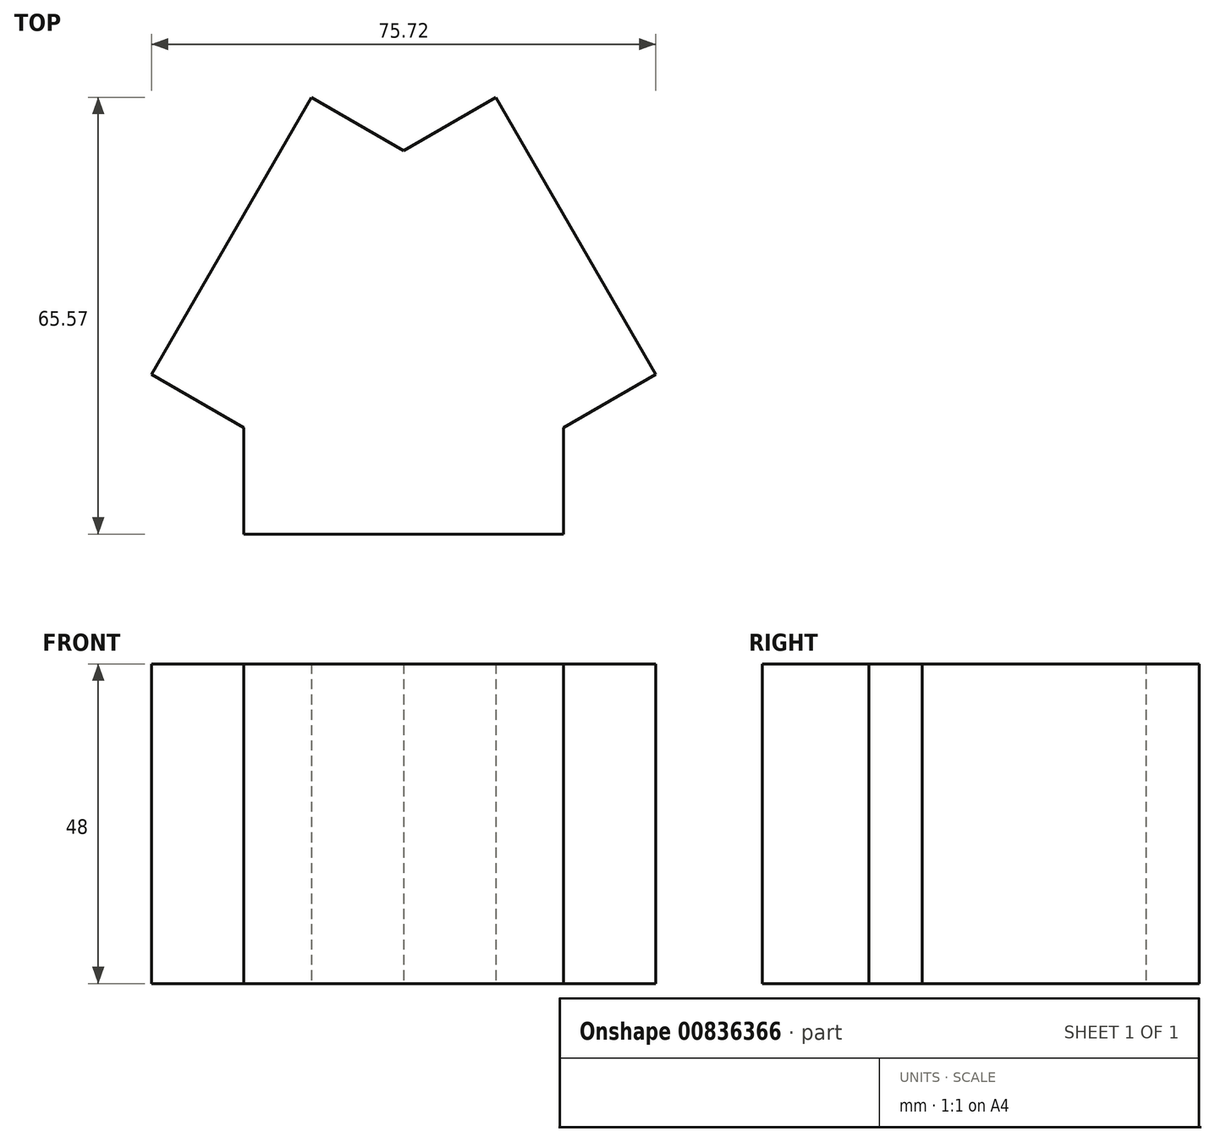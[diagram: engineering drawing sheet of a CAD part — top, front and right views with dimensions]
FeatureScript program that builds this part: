
annotation { "Feature Type Name" : "Feature", "Feature Type Description" : "" }
export const myFeature = defineFeature(function(context is Context, id is Id, definition is map)
    precondition{}
    {
        {
            var Q0;
            Q0=qCreatedBy(makeId("Top.planeOp"),FACE);
            var sketch = newSketch(context, id + "F0", { "sketchPlane" : qUnion([Q0])});
            skCircle(sketch, "E0.cCircle", {"center": v(0, 0) * mm, "radius": 13.86 * mm, "construction": true});
            skLineSegment(sketch, "E0.0", {"start": v(0, 27.71) * mm, "end": v(24, -13.86) * mm});
            skLineSegment(sketch, "E0.1", {"start": v(24, -13.86) * mm, "end": v(-24, -13.86) * mm});
            skLineSegment(sketch, "E0.2", {"start": v(-24, -13.86) * mm, "end": v(0, 27.71) * mm});
            skPoint(sketch, "E0.0.midPoint", {"position": v(12, 6.93) * mm});
            skSolve(sketch);
        }
        {
            var Q0;
            Q0=makeQuery(id+"F0.imprint","IMPRINT",FACE,{"disambiguationData":[TD([[makeQuery(id+"F0.imprint","IMPRINT",EDGE,{"derivedFrom":sQuery(id+"F0.wireOp",EDGE,"E0.0")}),-1.0]])]});
            extrude(context, id + "F1", {"entities" : qUnion([Q0]), "endBound" : BoundingType.SYMMETRIC, "depth" : 48 * mm, "offsetDistance" : 25 * mm});
        }
        {
            var Q0;
            Q0=makeQuery(id+"F1.opExtrude","SWEPT_FACE",FACE,{"disambiguationData":[OSD([sQuery(id+"F0.wireOp",EDGE,"E0.1")])]});
            extrude(context, id + "F2", {"entities" : qUnion([Q0]), "operationType" : NewBodyOperationType.ADD, "depth" : 16 * mm, "offsetDistance" : 25 * mm});
        }
        {
            var Q0;
            Q0=makeQuery(id+"F1.opExtrude","SWEPT_FACE",FACE,{"disambiguationData":[OSD([sQuery(id+"F0.wireOp",EDGE,"E0.0")])]});
            extrude(context, id + "F3", {"entities" : qUnion([Q0]), "operationType" : NewBodyOperationType.ADD, "depth" : 16 * mm, "offsetDistance" : 25 * mm});
        }
        {
            var Q0;
            Q0=makeQuery(id+"F1.opExtrude","SWEPT_FACE",FACE,{"disambiguationData":[OSD([sQuery(id+"F0.wireOp",EDGE,"E0.2")])]});
            extrude(context, id + "F4", {"entities" : qUnion([Q0]), "operationType" : NewBodyOperationType.ADD, "depth" : 16 * mm, "offsetDistance" : 25 * mm});
        }
        {
            var Q0;
            {var subQ0=sQuery(id+"F0.wireOp",EDGE,"E0.2");var subQ1=sQuery(id+"F0.wireOp",EDGE,"E0.0");var subQ2=sQuery(id+"F0.wireOp",EDGE,"E0.1");Q0=makeQuery(id+"F4.boolean.opBoolean","MERGE",FACE,{"derivedFrom":[makeQuery(id+"F3.boolean.opBoolean","MERGE",FACE,{"derivedFrom":[makeQuery(id+"F2.boolean.opBoolean","MERGE",FACE,{"derivedFrom":[makeQuery(id+"F1.opExtrude","CAP_FACE",FACE,{"disambiguationData":[OSD([subQ1,subQ2,subQ0])],"isStart":false}),makeQuery(id+"F2.opExtrude","SWEPT_FACE",FACE,{"disambiguationData":[OSD([subQ2]),TDD([makeQuery(id+"F1.opExtrude","CAP_EDGE",EDGE,{"disambiguationData":[OSD([subQ2])],"isStart":false})])]})]}),makeQuery(id+"F3.opExtrude","SWEPT_FACE",FACE,{"disambiguationData":[OSD([subQ1]),TDD([makeQuery(id+"F1.opExtrude","CAP_EDGE",EDGE,{"disambiguationData":[OSD([subQ1])],"isStart":false})])]})]}),makeQuery(id+"F4.opExtrude","SWEPT_FACE",FACE,{"disambiguationData":[OSD([subQ0]),TDD([makeQuery(id+"F1.opExtrude","CAP_EDGE",EDGE,{"disambiguationData":[OSD([subQ0])],"isStart":false})])]})]});}
            var Q1;
            {var subQ0=sQuery(id+"F0.wireOp",EDGE,"E0.2");var subQ1=sQuery(id+"F0.wireOp",EDGE,"E0.0");var subQ2=sQuery(id+"F0.wireOp",EDGE,"E0.1");Q1=makeQuery(id+"F4.boolean.opBoolean","MERGE",FACE,{"derivedFrom":[makeQuery(id+"F3.boolean.opBoolean","MERGE",FACE,{"derivedFrom":[makeQuery(id+"F2.boolean.opBoolean","MERGE",FACE,{"derivedFrom":[makeQuery(id+"F1.opExtrude","CAP_FACE",FACE,{"disambiguationData":[OSD([subQ1,subQ2,subQ0])],"isStart":true}),makeQuery(id+"F2.opExtrude","SWEPT_FACE",FACE,{"disambiguationData":[OSD([subQ2]),TDD([makeQuery(id+"F1.opExtrude","CAP_EDGE",EDGE,{"disambiguationData":[OSD([subQ2])],"isStart":true})])]})]}),makeQuery(id+"F3.opExtrude","SWEPT_FACE",FACE,{"disambiguationData":[OSD([subQ1]),TDD([makeQuery(id+"F1.opExtrude","CAP_EDGE",EDGE,{"disambiguationData":[OSD([subQ1])],"isStart":true})])]})]}),makeQuery(id+"F4.opExtrude","SWEPT_FACE",FACE,{"disambiguationData":[OSD([subQ0]),TDD([makeQuery(id+"F1.opExtrude","CAP_EDGE",EDGE,{"disambiguationData":[OSD([subQ0])],"isStart":true})])]})]});}
            cPlane(context, id + "F5", {"entities" : qUnion([Q0, Q1]), "cplaneType" : CPlaneType.MID_PLANE, "offset" : 25 * mm, "width" : 150 * mm, "height" : 150 * mm});
        }
    });
